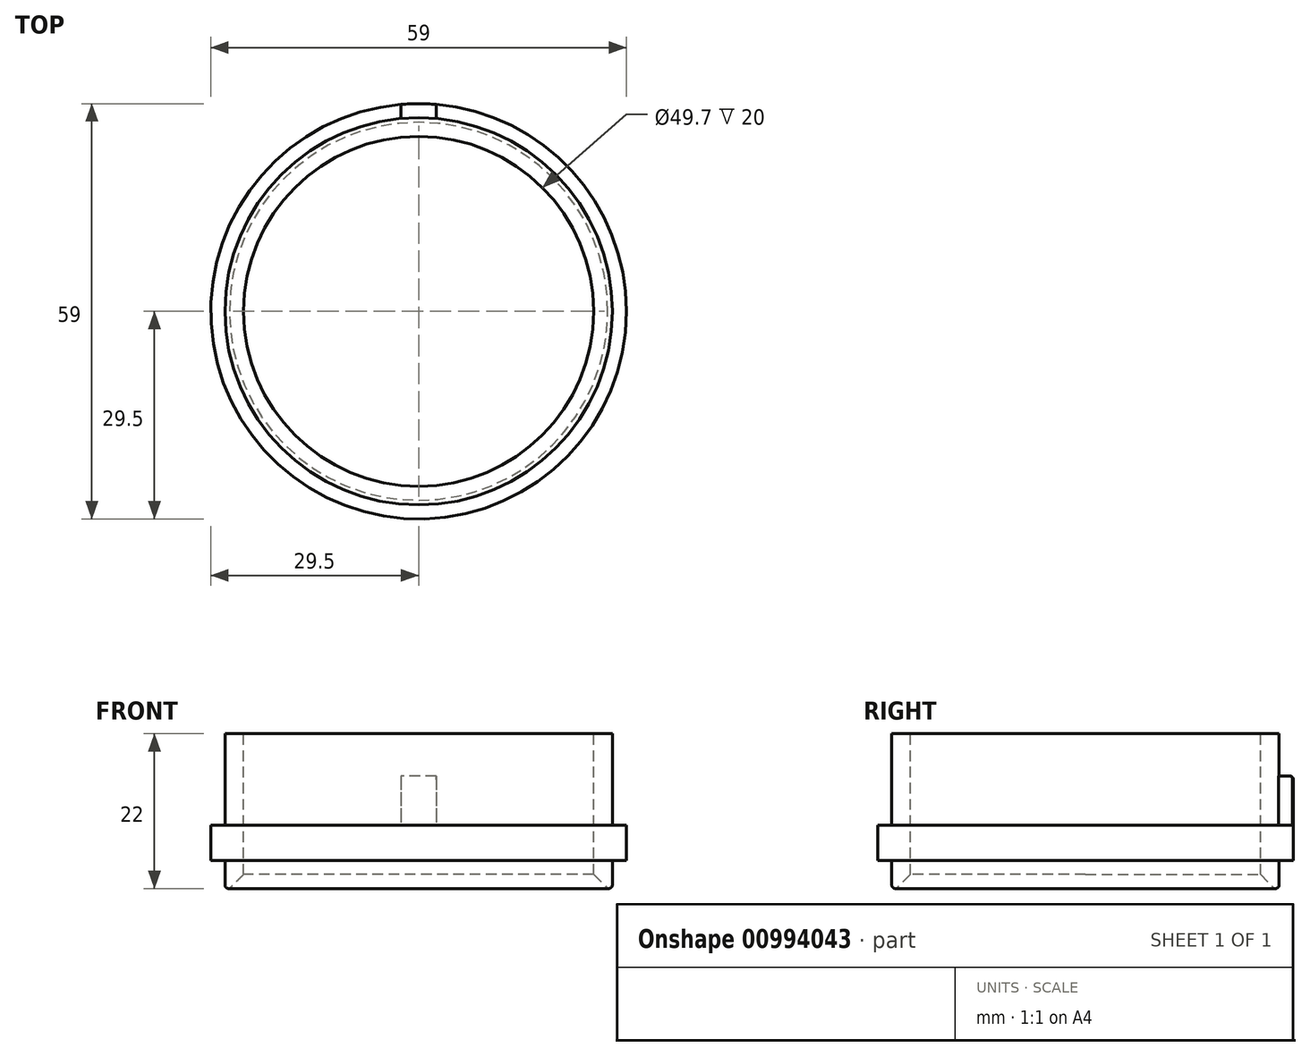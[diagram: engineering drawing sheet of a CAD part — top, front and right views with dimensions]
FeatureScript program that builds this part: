
annotation { "Feature Type Name" : "Feature", "Feature Type Description" : "" }
export const myFeature = defineFeature(function(context is Context, id is Id, definition is map)
    precondition{}
    {
        {
            var Q0;
            Q0=qCreatedBy(makeId("Front.planeOp"),FACE);
            var sketch = newSketch(context, id + "F0", { "sketchPlane" : qUnion([Q0])});
            skLineSegment(sketch, "E0", {"start": v(24.85, 0) * mm, "end": v(27.5, 0) * mm});
            skLineSegment(sketch, "E1", {"start": v(29.5, -18) * mm, "end": v(27.5, -18) * mm});
            skLineSegment(sketch, "E2", {"start": v(27.5, -18) * mm, "end": v(27.5, -22) * mm});
            skLineSegment(sketch, "E3", {"start": v(27.5, -22) * mm, "end": v(24.85, -22) * mm});
            skLineSegment(sketch, "E4", {"start": v(24.85, -22) * mm, "end": v(24.85, 0) * mm});
            skLineSegment(sketch, "E5", {"start": v(0, 0) * mm, "end": v(0, -12.37) * mm, "construction": true});
            skLineSegment(sketch, "E6", {"start": v(29.5, -18) * mm, "end": v(29.5, -13) * mm});
            skLineSegment(sketch, "E7", {"start": v(29.5, -13) * mm, "end": v(27.5, -13) * mm});
            skLineSegment(sketch, "E8", {"start": v(27.5, -13) * mm, "end": v(27.5, 0) * mm});
            skSolve(sketch);
        }
        {
            var Q0;
            Q0=makeQuery(id+"F0.imprint","IMPRINT",FACE,{"disambiguationData":[TD([[makeQuery(id+"F0.imprint","IMPRINT",EDGE,{"derivedFrom":sQuery(id+"F0.wireOp",EDGE,"E0")}),-1.0]])]});
            var Q1;
            Q1=sQuery(id+"F0.wireOp",EDGE,"E5");
            revolve(context, id + "F1", {"surfaceOperationType" : NewSurfaceOperationType.NEW, "entities" : qUnion([Q0]), "axis" : qUnion([Q1]), "revolveType" : RevolveType.FULL});
        }
        {
            var Q0;
            Q0=makeQuery(id+"F1.opRevolve","SWEPT_EDGE",EDGE,{"disambiguationData":[OSD([sQuery(id+"F0.wireOp",EDGE,"E2"),sQuery(id+"F0.wireOp",EDGE,"E3")])]});
            fillet(context, id + "F2", {"entities" : qUnion([Q0]), "radius" : .5 * mm, "tangentPropagation" : true, "allowEdgeOverflow" : false});
        }
        {
            var Q0;
            Q0=makeQuery(id+"F1.opRevolve","SWEPT_EDGE",EDGE,{"disambiguationData":[OSD([sQuery(id+"F0.wireOp",EDGE,"E3"),sQuery(id+"F0.wireOp",EDGE,"E4")])]});
            chamfer(context, id + "F3", {"entities" : qUnion([Q0]), "width" : 2 * mm, "tangentPropagation" : true});
        }
        {
            var Q0;
            Q0=makeQuery(id+"F1.opRevolve","SWEPT_FACE",FACE,{"disambiguationData":[OSD([sQuery(id+"F0.wireOp",EDGE,"E7")])]});
            var sketch = newSketch(context, id + "F4", { "sketchPlane" : qUnion([Q0])});
            skLineSegment(sketch, "E9", {"start": v(-2.5, 27.39) * mm, "end": v(-2.5, 29.4) * mm});
            skArc(sketch, "E10.0", {"start": v(2.5, 29.4) * mm, "mid": v(0, 29.5) * mm, "end": v(-2.5, 29.4) * mm});
            skLineSegment(sketch, "E11", {"start": v(2.5, 29.4) * mm, "end": v(2.5, 27.39) * mm});
            skLineSegment(sketch, "E12", {"start": v(-2.5, 27.39) * mm, "end": v(2.5, 27.39) * mm});
            skSolve(sketch);
        }
        {
            var Q0;
            Q0 = qSketchRegion(id + "F4", true);
            extrude(context, id + "F5", {"entities" : qUnion([Q0]), "operationType" : NewBodyOperationType.ADD, "depth" : 7 * mm, "offsetDistance" : 25 * mm});
        }
        {
            var Q0;
            Q0=makeQuery(id+"F5.opExtrude","CAP_EDGE",EDGE,{"disambiguationData":[OSD([sQuery(id+"F4.wireOp",EDGE,"E10.0")])],"isStart":false});
            fillet(context, id + "F6", {"entities" : qUnion([Q0]), "radius" : .5 * mm, "tangentPropagation" : true, "allowEdgeOverflow" : false});
        }
    });
